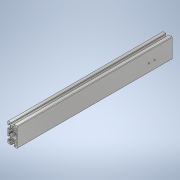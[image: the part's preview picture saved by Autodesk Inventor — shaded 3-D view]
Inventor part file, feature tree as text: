
AUTODESK INVENTOR PART (.ipt)
format: ipt  version: 2022 (Build 260153000, 153)  size: 312,320 bytes
history: native  units: mm
features: other x7, sketch x5, hole x4, pattern_linear x3, extrude x1
ambient origin geometry x8: Origin, YZ Plane, XZ Plane, XY Plane, X Axis, Y Axis, Z Axis, Center Point
bodies: Solid1 (feature_tree)
feature tree (20):
  extrude  "Extrusion1"  Depth=10.0mm TaperAngle=0.0deg
  hole  "Hole1"  [1 undecoded]
  pattern_linear  "Rectangular Pattern1"  Count1=2 Spacing1=10.0mm
  hole  "Hole2"  [1 undecoded]
  pattern_linear  "Rectangular Pattern2"  Spacing1=16.0mm  [1 undecoded]
  hole  "Hole3"  [1 undecoded]
  pattern_linear  "Rectangular Pattern3"  Spacing1=36.5mm  [1 undecoded]
  other  "C1_XY"
  other  "C1_YZ"
  other  "C1_ZX"
  other  "C1_X"
  other  "C1_Y"
  other  "C1_Z"
  other  "C1_Center"
  hole  "穴5"  [1 undecoded]
  sketch  "Sketch_63"  dims[d28=4.2mm d29=6.0mm d30=4.0mm d31=2.0mm d32=90.0deg d33=290.0mm d34=0.0mm d35=20.0mm d37=20.0mm d38=10.0mm d40=0.0mm d41=0.0mm d52=16.0mm d53=48.5mm d54=36.5mm d55=2.459mm d56=25.0mm d57=3.023mm d58=2.0mm d59=14.3117mm d60=8.8mm d61=20.594885mm]
  sketch  "Sketch2"  dims[d0=320.0mm d1=0.0mm]
  sketch  "Sketch3"  dims[d2=4.134mm d3=15.0mm d4=5.0mm d5=2.0mm d6=90.0deg d7=15.0mm d8=0.0mm d9=20.0mm d11=20.0mm d12=10.0mm d14=0.0mm]
  sketch  "Sketch4"  dims[d15=4.134mm d16=15.0mm d17=5.0mm d18=2.0mm d19=90.0deg d20=15.0mm d21=0.0mm d22=20.0mm d24=20.0mm d25=10.0mm d27=0.0mm]
  sketch  "スケッチ7"
note: 6 required parameter values undecoded (feature->parameter linkage not recoverable at this tier; creation-order binding heuristic only, values carry confidence <= 0.55)
